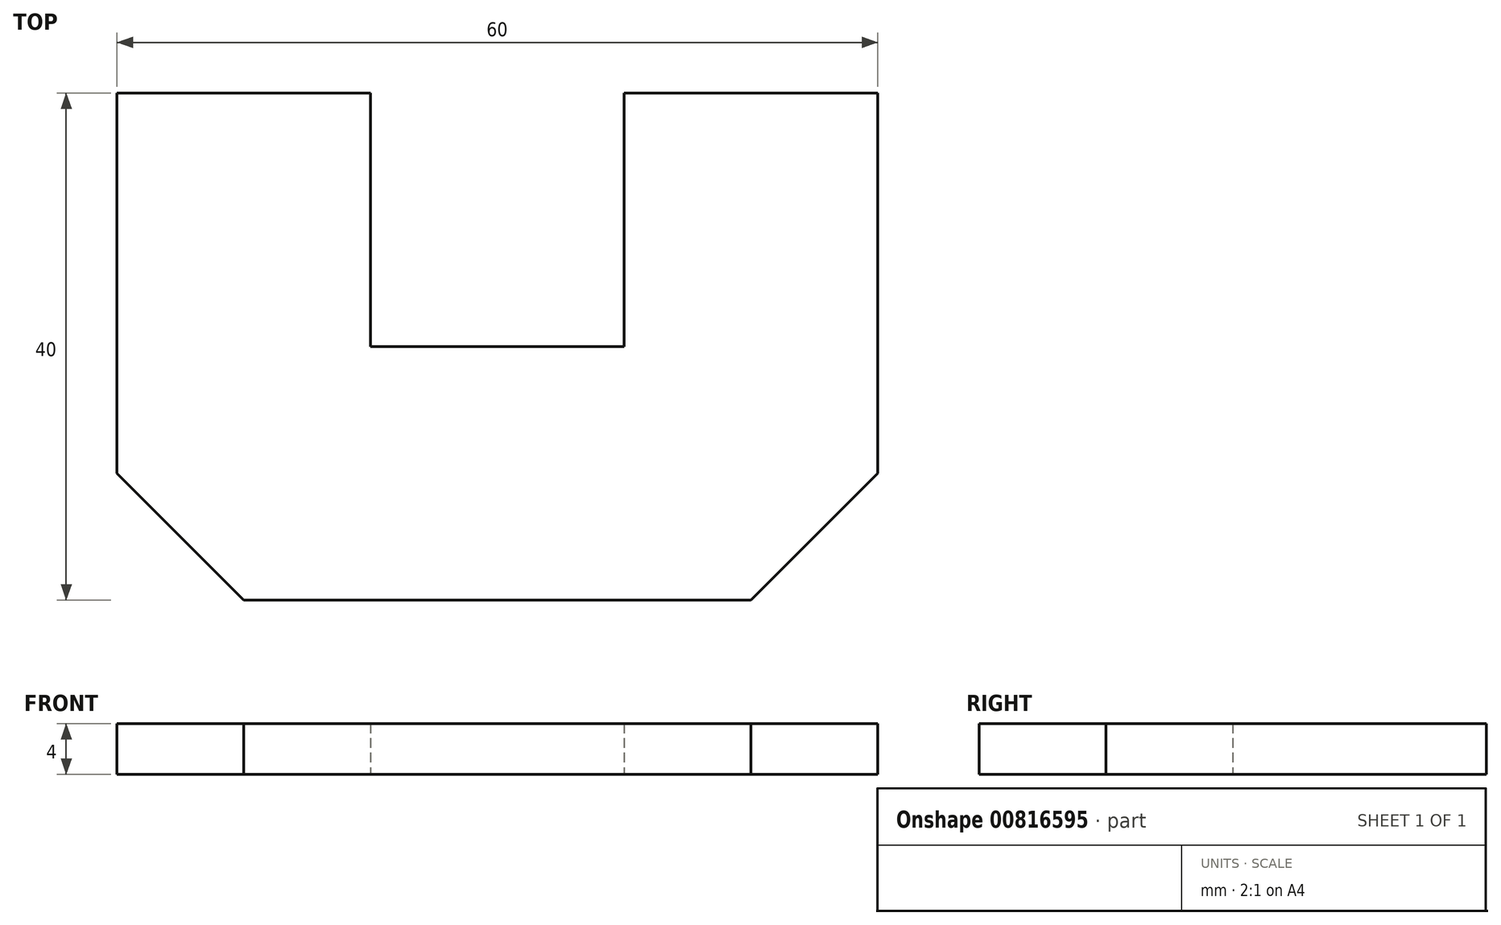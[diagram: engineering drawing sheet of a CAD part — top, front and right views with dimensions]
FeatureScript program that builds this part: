
annotation { "Feature Type Name" : "Feature", "Feature Type Description" : "" }
export const myFeature = defineFeature(function(context is Context, id is Id, definition is map)
    precondition{}
    {
        {
            var Q0;
            Q0=qCreatedBy(makeId("Top.planeOp"),FACE);
            var sketch = newSketch(context, id + "F0", { "sketchPlane" : qUnion([Q0])});
            skLineSegment(sketch, "E0.bottom", {"start": v(-30, 20) * mm, "end": v(30, 20) * mm});
            skLineSegment(sketch, "E0.top", {"start": v(-30, -20) * mm, "end": v(30, -20) * mm});
            skLineSegment(sketch, "E0.left", {"start": v(-30, 20) * mm, "end": v(-30, -20) * mm});
            skLineSegment(sketch, "E0.right", {"start": v(30, 20) * mm, "end": v(30, -20) * mm});
            skLineSegment(sketch, "E1", {"start": v(0, 20) * mm, "end": v(0, -20) * mm, "construction": true});
            skLineSegment(sketch, "E2.bottom", {"start": v(-10, 20) * mm, "end": v(10, 20) * mm});
            skLineSegment(sketch, "E2.top", {"start": v(-10, 0) * mm, "end": v(10, 0) * mm});
            skLineSegment(sketch, "E2.left", {"start": v(-10, 20) * mm, "end": v(-10, 0) * mm});
            skLineSegment(sketch, "E2.right", {"start": v(10, 20) * mm, "end": v(10, 0) * mm});
            skLineSegment(sketch, "E3", {"start": v(-30, -10) * mm, "end": v(-20, -20) * mm});
            skLineSegment(sketch, "E4.MirrorCS", {"start": v(30, -10) * mm, "end": v(20, -20) * mm});
            skSolve(sketch);
        }
        {
            var Q0;
            Q0=makeQuery(id+"F0.imprint","IMPRINT",FACE,{"disambiguationData":[TD([[makeQuery(id+"F0.imprint","IMPRINT",EDGE,{"derivedFrom":sQuery(id+"F0.wireOp",EDGE,"E2.top")}),-1.0]])]});
            extrude(context, id + "F1", {"entities" : qUnion([Q0]), "depth" : 4 * mm, "offsetDistance" : 25 * mm});
        }
    });
